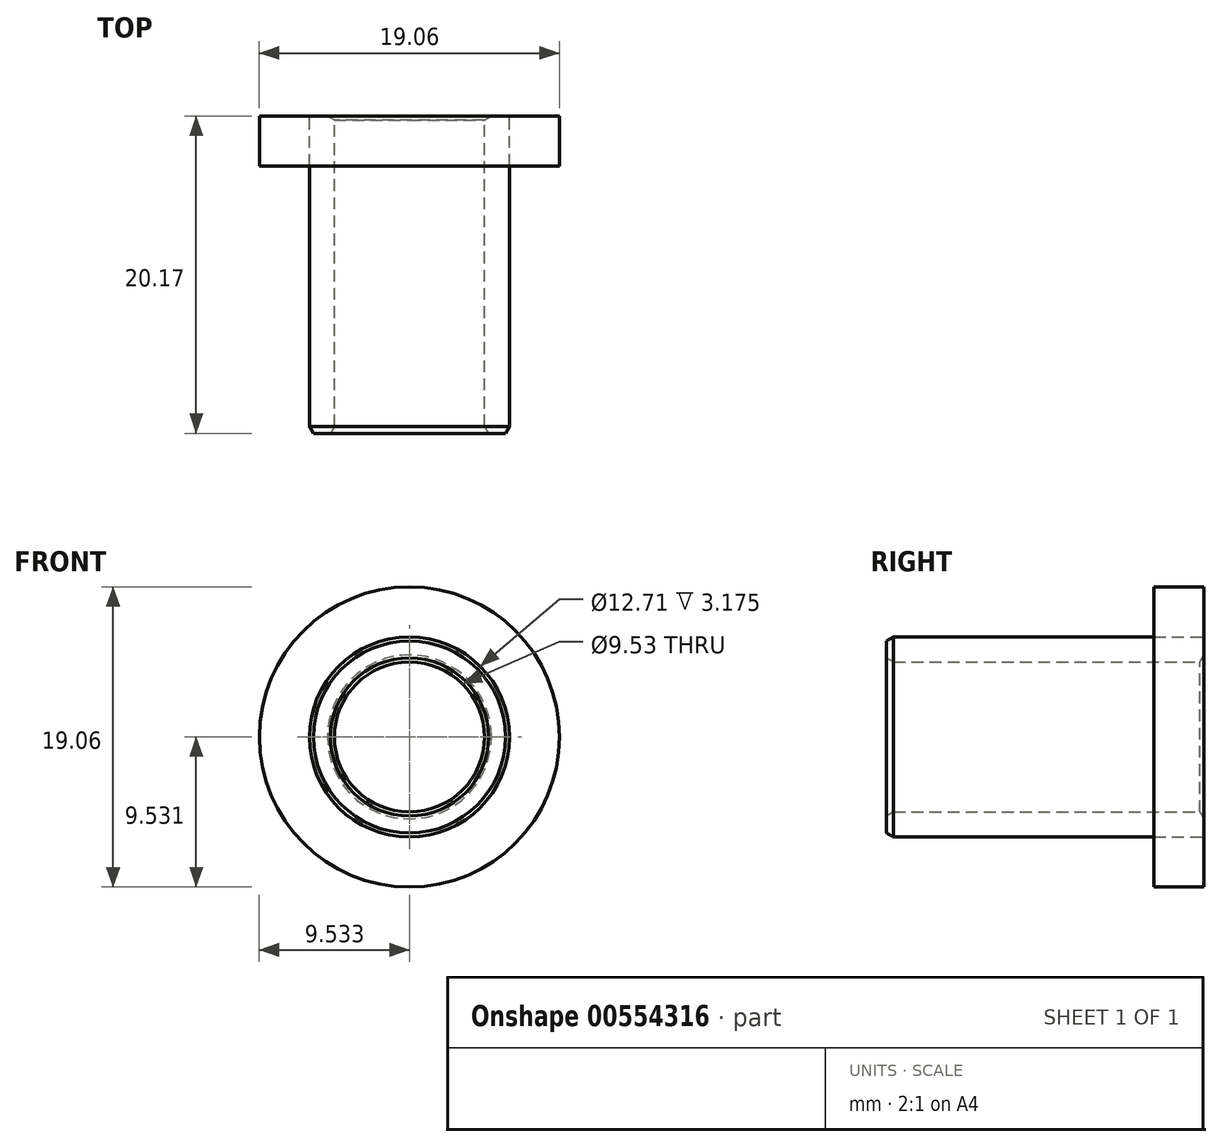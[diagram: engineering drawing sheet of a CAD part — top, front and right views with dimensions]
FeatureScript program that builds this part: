
annotation { "Feature Type Name" : "Feature", "Feature Type Description" : "" }
export const myFeature = defineFeature(function(context is Context, id is Id, definition is map)
    precondition{}
    {
        {
            var Q0;
            Q0=qCreatedBy(makeId("Front.planeOp"),FACE);
            var sketch = newSketch(context, id + "F0", { "sketchPlane" : qUnion([Q0])});
            skCircle(sketch, "E0", {"center": v(0, 0) * mm, "radius": 0.37 * mm});
            skCircle(sketch, "E1", {"center": v(-20.29, 11.8) * mm, "radius": 9.53 * mm});
            skCircle(sketch, "E2", {"center": v(-20.29, 11.8) * mm, "radius": 6.35 * mm});
            skCircle(sketch, "E3", {"center": v(-20.29, 11.8) * mm, "radius": 4.77 * mm});
            skSolve(sketch);
        }
        {
            var Q0;
            Q0=makeQuery(id+"F0.imprint","IMPRINT",FACE,{"disambiguationData":[TD([[makeQuery(id+"F0.imprint","IMPRINT",EDGE,{"derivedFrom":sQuery(id+"F0.wireOp",EDGE,"E2")}),1.0]])]});
            extrude(context, id + "F1", {"entities" : qUnion([Q0]), "depth" : 20.17 * mm, "offsetDistance" : 25.4 * mm});
        }
        {
            var Q0;
            Q0=makeQuery(id+"F0.imprint","IMPRINT",FACE,{"disambiguationData":[TD([[makeQuery(id+"F0.imprint","IMPRINT",EDGE,{"derivedFrom":sQuery(id+"F0.wireOp",EDGE,"E1")}),1.0]])]});
            extrude(context, id + "F2", {"entities" : qUnion([Q0]), "depth" : 3.17 * mm, "offsetDistance" : 25.4 * mm});
        }
        {
            var Q0;
            Q0=makeQuery(id+"F1.opExtrude","CAP_EDGE",EDGE,{"disambiguationData":[OSD([sQuery(id+"F0.wireOp",EDGE,"E2")])],"isStart":false});
            chamfer(context, id + "F3", {"entities" : qUnion([Q0]), "chamferType" : ChamferType.OFFSET_ANGLE, "width" : 0.25 * mm, "oppositeDirection" : false, "angle" : 60 * degree, "tangentPropagation" : true});
        }
        {
            var Q0;
            Q0=makeQuery(id+"F1.opExtrude","CAP_EDGE",EDGE,{"disambiguationData":[OSD([sQuery(id+"F0.wireOp",EDGE,"E3")])],"isStart":false});
            chamfer(context, id + "F4", {"entities" : qUnion([Q0]), "chamferType" : ChamferType.OFFSET_ANGLE, "width" : 0.25 * mm, "oppositeDirection" : true, "angle" : 60 * degree, "tangentPropagation" : true});
        }
        {
            var Q0;
            Q0=makeQuery(id+"F1.opExtrude","CAP_EDGE",EDGE,{"disambiguationData":[OSD([sQuery(id+"F0.wireOp",EDGE,"E3")])],"isStart":true});
            chamfer(context, id + "F5", {"entities" : qUnion([Q0]), "chamferType" : ChamferType.OFFSET_ANGLE, "width" : 0.25 * mm, "oppositeDirection" : true, "angle" : 60 * degree, "tangentPropagation" : true});
        }
    });
